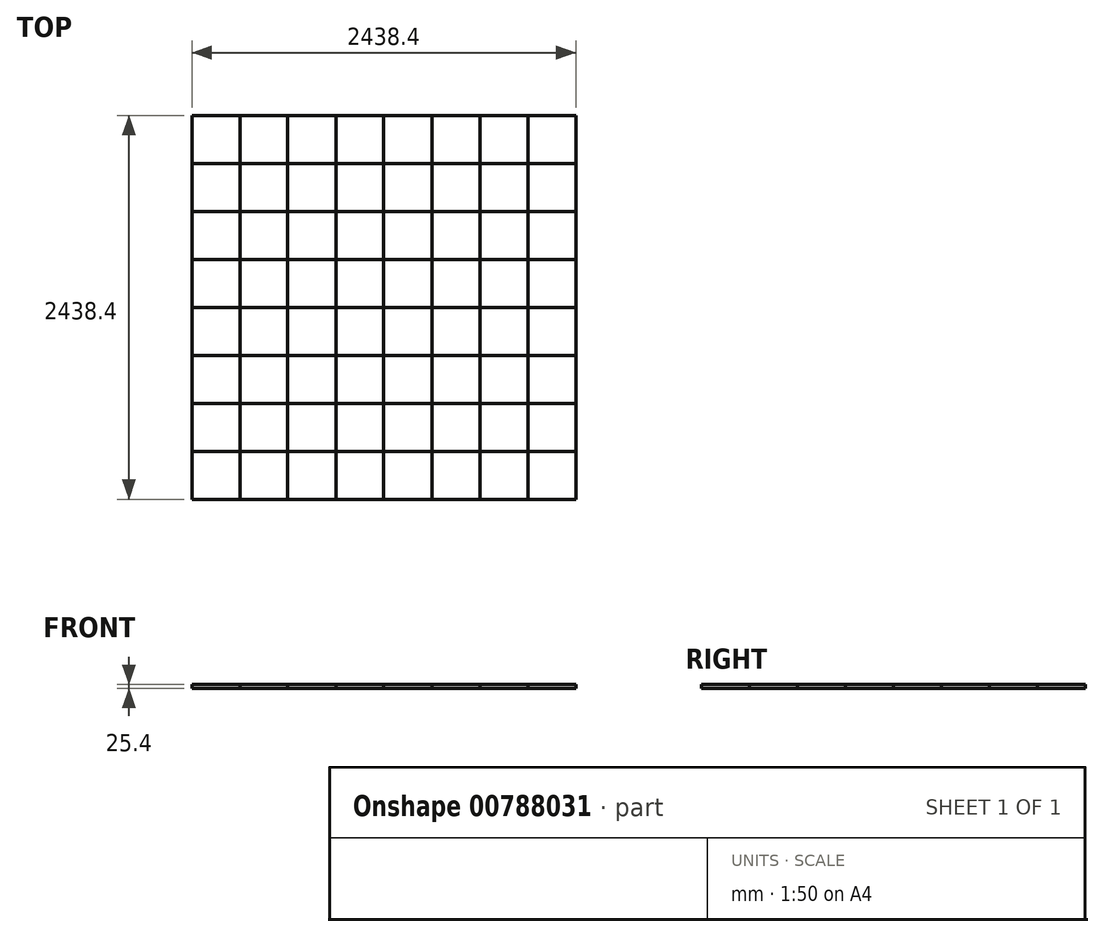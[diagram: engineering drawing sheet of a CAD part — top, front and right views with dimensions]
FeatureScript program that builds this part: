
annotation { "Feature Type Name" : "Feature", "Feature Type Description" : "" }
export const myFeature = defineFeature(function(context is Context, id is Id, definition is map)
    precondition{}
    {
        {
            var Q0;
            Q0=qCreatedBy(makeId("Top.planeOp"),FACE);
            var sketch = newSketch(context, id + "F0", { "sketchPlane" : qUnion([Q0])});
            skLineSegment(sketch, "E0.bottom", {"start": v(-1218.73, 1220.27) * mm, "end": v(1219.67, 1220.27) * mm});
            skLineSegment(sketch, "E0.top", {"start": v(-1218.73, -1218.13) * mm, "end": v(1219.67, -1218.13) * mm});
            skLineSegment(sketch, "E0.left", {"start": v(-1218.73, 1220.27) * mm, "end": v(-1218.73, -1218.13) * mm});
            skLineSegment(sketch, "E0.right", {"start": v(1219.67, 1220.27) * mm, "end": v(1219.67, -1218.13) * mm});
            skLineSegment(sketch, "E1", {"start": v(-913.93, -1218.13) * mm, "end": v(-913.93, 1220.27) * mm});
            skLineSegment(sketch, "E2", {"start": v(-609.13, 1229.92) * mm, "end": v(-609.13, -1218.13) * mm});
            skLineSegment(sketch, "E3", {"start": v(-304.33, -1218.13) * mm, "end": v(-304.33, 1220.27) * mm});
            skLineSegment(sketch, "E4", {"start": v(-609.13, 1220.27) * mm, "end": v(-609.13, -1218.13) * mm});
            skLineSegment(sketch, "E5", {"start": v(0.47, -1218.13) * mm, "end": v(0.47, 1220.27) * mm});
            skLineSegment(sketch, "E6", {"start": v(305.27, 1220.27) * mm, "end": v(305.27, -1218.13) * mm});
            skLineSegment(sketch, "E7", {"start": v(610.07, -1218.13) * mm, "end": v(610.07, 1220.27) * mm});
            skLineSegment(sketch, "E8", {"start": v(914.87, -1218.13) * mm, "end": v(914.87, 1220.27) * mm});
            skLineSegment(sketch, "E9", {"start": v(-1218.73, 915.47) * mm, "end": v(1219.67, 915.47) * mm});
            skLineSegment(sketch, "E10", {"start": v(1219.67, 610.67) * mm, "end": v(-1218.73, 610.67) * mm});
            skLineSegment(sketch, "E11", {"start": v(-1218.73, 305.87) * mm, "end": v(1219.67, 305.87) * mm});
            skLineSegment(sketch, "E12", {"start": v(1219.67, 1.07) * mm, "end": v(-1218.73, 1.07) * mm});
            skLineSegment(sketch, "E13", {"start": v(-1218.73, -303.73) * mm, "end": v(1219.67, -303.73) * mm});
            skLineSegment(sketch, "E14", {"start": v(1219.67, -608.53) * mm, "end": v(-1218.73, -608.53) * mm});
            skLineSegment(sketch, "E15", {"start": v(-1218.73, -913.33) * mm, "end": v(1219.67, -913.33) * mm});
            skSolve(sketch);
        }
        {
            var Q0;
            {var subQ0=sQuery(id+"F0.wireOp",EDGE,"E0.left");var subQ1=sQuery(id+"F0.wireOp",EDGE,"E0.top");var subQ2=makeQuery(id+"F0.imprint","INTERSECT",VERTEX,{"derivedFrom":[subQ1,subQ0]});Q0=makeQuery(id+"F0.imprint","IMPRINT",FACE,{"disambiguationData":[TD([[makeQuery(id+"F0.imprint","IMPRINT",EDGE,{"disambiguationData":[TD([[subQ2,-1.0]])],"derivedFrom":subQ1}),1.0]])]});}
            var Q1;
            {var subQ0=sQuery(id+"F0.wireOp",EDGE,"E15");var subQ1=sQuery(id+"F0.wireOp",EDGE,"E1");var subQ2=makeQuery(id+"F0.imprint","INTERSECT",VERTEX,{"derivedFrom":[subQ1,subQ0]});Q1=makeQuery(id+"F0.imprint","IMPRINT",FACE,{"disambiguationData":[TD([[makeQuery(id+"F0.imprint","IMPRINT",EDGE,{"disambiguationData":[TD([[subQ2,-1.0]])],"derivedFrom":subQ1}),-1.0]])]});}
            var Q2;
            {var subQ0=sQuery(id+"F0.wireOp",EDGE,"E3");var subQ1=sQuery(id+"F0.wireOp",EDGE,"E0.top");var subQ2=makeQuery(id+"F0.imprint","INTERSECT",VERTEX,{"derivedFrom":[subQ1,subQ0]});Q2=makeQuery(id+"F0.imprint","IMPRINT",FACE,{"disambiguationData":[TD([[makeQuery(id+"F0.imprint","IMPRINT",EDGE,{"disambiguationData":[TD([[subQ2,1.0]])],"derivedFrom":subQ1}),1.0]])]});}
            var Q3;
            {var subQ0=sQuery(id+"F0.wireOp",EDGE,"E15");var subQ1=sQuery(id+"F0.wireOp",EDGE,"E3");var subQ2=makeQuery(id+"F0.imprint","INTERSECT",VERTEX,{"derivedFrom":[subQ1,subQ0]});Q3=makeQuery(id+"F0.imprint","IMPRINT",FACE,{"disambiguationData":[TD([[makeQuery(id+"F0.imprint","IMPRINT",EDGE,{"disambiguationData":[TD([[subQ2,-1.0]])],"derivedFrom":subQ1}),-1.0]])]});}
            var Q4;
            {var subQ0=sQuery(id+"F0.wireOp",EDGE,"E5");var subQ1=sQuery(id+"F0.wireOp",EDGE,"E0.top");var subQ2=makeQuery(id+"F0.imprint","INTERSECT",VERTEX,{"derivedFrom":[subQ1,subQ0]});Q4=makeQuery(id+"F0.imprint","IMPRINT",FACE,{"disambiguationData":[TD([[makeQuery(id+"F0.imprint","IMPRINT",EDGE,{"disambiguationData":[TD([[subQ2,-1.0]])],"derivedFrom":subQ1}),1.0]])]});}
            var Q5;
            {var subQ0=sQuery(id+"F0.wireOp",EDGE,"E14");var subQ1=sQuery(id+"F0.wireOp",EDGE,"E6");var subQ2=makeQuery(id+"F0.imprint","INTERSECT",VERTEX,{"derivedFrom":[subQ1,subQ0]});Q5=makeQuery(id+"F0.imprint","IMPRINT",FACE,{"disambiguationData":[TD([[makeQuery(id+"F0.imprint","IMPRINT",EDGE,{"disambiguationData":[TD([[subQ2,-1.0]])],"derivedFrom":subQ1}),1.0]])]});}
            var Q6;
            {var subQ0=sQuery(id+"F0.wireOp",EDGE,"E7");var subQ1=sQuery(id+"F0.wireOp",EDGE,"E0.top");var subQ2=makeQuery(id+"F0.imprint","INTERSECT",VERTEX,{"derivedFrom":[subQ1,subQ0]});Q6=makeQuery(id+"F0.imprint","IMPRINT",FACE,{"disambiguationData":[TD([[makeQuery(id+"F0.imprint","IMPRINT",EDGE,{"disambiguationData":[TD([[subQ2,-1.0]])],"derivedFrom":subQ1}),1.0]])]});}
            var Q7;
            {var subQ0=sQuery(id+"F0.wireOp",EDGE,"E14");var subQ1=sQuery(id+"F0.wireOp",EDGE,"E0.right");var subQ2=makeQuery(id+"F0.imprint","INTERSECT",VERTEX,{"derivedFrom":[subQ1,subQ0]});Q7=makeQuery(id+"F0.imprint","IMPRINT",FACE,{"disambiguationData":[TD([[makeQuery(id+"F0.imprint","IMPRINT",EDGE,{"disambiguationData":[TD([[subQ2,-1.0]])],"derivedFrom":subQ1}),-1.0]])]});}
            var Q8;
            {var subQ0=sQuery(id+"F0.wireOp",EDGE,"E14");var subQ1=sQuery(id+"F0.wireOp",EDGE,"E7");var subQ2=makeQuery(id+"F0.imprint","INTERSECT",VERTEX,{"derivedFrom":[subQ1,subQ0]});Q8=makeQuery(id+"F0.imprint","IMPRINT",FACE,{"disambiguationData":[TD([[makeQuery(id+"F0.imprint","IMPRINT",EDGE,{"disambiguationData":[TD([[subQ2,-1.0]])],"derivedFrom":subQ1}),-1.0]])]});}
            var Q9;
            {var subQ0=sQuery(id+"F0.wireOp",EDGE,"E14");var subQ1=sQuery(id+"F0.wireOp",EDGE,"E5");var subQ2=makeQuery(id+"F0.imprint","INTERSECT",VERTEX,{"derivedFrom":[subQ1,subQ0]});Q9=makeQuery(id+"F0.imprint","IMPRINT",FACE,{"disambiguationData":[TD([[makeQuery(id+"F0.imprint","IMPRINT",EDGE,{"disambiguationData":[TD([[subQ2,-1.0]])],"derivedFrom":subQ1}),-1.0]])]});}
            var Q10;
            {var subQ0=sQuery(id+"F0.wireOp",EDGE,"E14");var subQ1=sQuery(id+"F0.wireOp",EDGE,"E3");var subQ2=makeQuery(id+"F0.imprint","INTERSECT",VERTEX,{"derivedFrom":[subQ1,subQ0]});Q10=makeQuery(id+"F0.imprint","IMPRINT",FACE,{"disambiguationData":[TD([[makeQuery(id+"F0.imprint","IMPRINT",EDGE,{"disambiguationData":[TD([[subQ2,-1.0]])],"derivedFrom":subQ1}),1.0]])]});}
            var Q11;
            {var subQ0=sQuery(id+"F0.wireOp",EDGE,"E13");var subQ1=sQuery(id+"F0.wireOp",EDGE,"E0.left");var subQ2=makeQuery(id+"F0.imprint","INTERSECT",VERTEX,{"derivedFrom":[subQ1,subQ0]});Q11=makeQuery(id+"F0.imprint","IMPRINT",FACE,{"disambiguationData":[TD([[makeQuery(id+"F0.imprint","IMPRINT",EDGE,{"disambiguationData":[TD([[subQ2,-1.0]])],"derivedFrom":subQ1}),1.0]])]});}
            var Q12;
            {var subQ0=sQuery(id+"F0.wireOp",EDGE,"E13");var subQ1=sQuery(id+"F0.wireOp",EDGE,"E1");var subQ2=makeQuery(id+"F0.imprint","INTERSECT",VERTEX,{"derivedFrom":[subQ1,subQ0]});Q12=makeQuery(id+"F0.imprint","IMPRINT",FACE,{"disambiguationData":[TD([[makeQuery(id+"F0.imprint","IMPRINT",EDGE,{"disambiguationData":[TD([[subQ2,-1.0]])],"derivedFrom":subQ1}),-1.0]])]});}
            var Q13;
            {var subQ0=sQuery(id+"F0.wireOp",EDGE,"E13");var subQ1=sQuery(id+"F0.wireOp",EDGE,"E3");var subQ2=makeQuery(id+"F0.imprint","INTERSECT",VERTEX,{"derivedFrom":[subQ1,subQ0]});Q13=makeQuery(id+"F0.imprint","IMPRINT",FACE,{"disambiguationData":[TD([[makeQuery(id+"F0.imprint","IMPRINT",EDGE,{"disambiguationData":[TD([[subQ2,-1.0]])],"derivedFrom":subQ1}),-1.0]])]});}
            var Q14;
            {var subQ0=sQuery(id+"F0.wireOp",EDGE,"E12");var subQ1=sQuery(id+"F0.wireOp",EDGE,"E6");var subQ2=makeQuery(id+"F0.imprint","INTERSECT",VERTEX,{"derivedFrom":[subQ1,subQ0]});Q14=makeQuery(id+"F0.imprint","IMPRINT",FACE,{"disambiguationData":[TD([[makeQuery(id+"F0.imprint","IMPRINT",EDGE,{"disambiguationData":[TD([[subQ2,-1.0]])],"derivedFrom":subQ1}),1.0]])]});}
            var Q15;
            {var subQ0=sQuery(id+"F0.wireOp",EDGE,"E12");var subQ1=sQuery(id+"F0.wireOp",EDGE,"E0.right");var subQ2=makeQuery(id+"F0.imprint","INTERSECT",VERTEX,{"derivedFrom":[subQ1,subQ0]});Q15=makeQuery(id+"F0.imprint","IMPRINT",FACE,{"disambiguationData":[TD([[makeQuery(id+"F0.imprint","IMPRINT",EDGE,{"disambiguationData":[TD([[subQ2,-1.0]])],"derivedFrom":subQ1}),-1.0]])]});}
            var Q16;
            {var subQ0=sQuery(id+"F0.wireOp",EDGE,"E12");var subQ1=sQuery(id+"F0.wireOp",EDGE,"E7");var subQ2=makeQuery(id+"F0.imprint","INTERSECT",VERTEX,{"derivedFrom":[subQ1,subQ0]});Q16=makeQuery(id+"F0.imprint","IMPRINT",FACE,{"disambiguationData":[TD([[makeQuery(id+"F0.imprint","IMPRINT",EDGE,{"disambiguationData":[TD([[subQ2,-1.0]])],"derivedFrom":subQ1}),-1.0]])]});}
            var Q17;
            {var subQ0=sQuery(id+"F0.wireOp",EDGE,"E10");var subQ1=sQuery(id+"F0.wireOp",EDGE,"E0.right");var subQ2=makeQuery(id+"F0.imprint","INTERSECT",VERTEX,{"derivedFrom":[subQ1,subQ0]});Q17=makeQuery(id+"F0.imprint","IMPRINT",FACE,{"disambiguationData":[TD([[makeQuery(id+"F0.imprint","IMPRINT",EDGE,{"disambiguationData":[TD([[subQ2,-1.0]])],"derivedFrom":subQ1}),-1.0]])]});}
            var Q18;
            {var subQ0=sQuery(id+"F0.wireOp",EDGE,"E10");var subQ1=sQuery(id+"F0.wireOp",EDGE,"E7");var subQ2=makeQuery(id+"F0.imprint","INTERSECT",VERTEX,{"derivedFrom":[subQ1,subQ0]});Q18=makeQuery(id+"F0.imprint","IMPRINT",FACE,{"disambiguationData":[TD([[makeQuery(id+"F0.imprint","IMPRINT",EDGE,{"disambiguationData":[TD([[subQ2,-1.0]])],"derivedFrom":subQ1}),-1.0]])]});}
            var Q19;
            {var subQ0=sQuery(id+"F0.wireOp",EDGE,"E0.right");var subQ1=sQuery(id+"F0.wireOp",EDGE,"E0.bottom");var subQ2=makeQuery(id+"F0.imprint","INTERSECT",VERTEX,{"derivedFrom":[subQ1,subQ0]});Q19=makeQuery(id+"F0.imprint","IMPRINT",FACE,{"disambiguationData":[TD([[makeQuery(id+"F0.imprint","IMPRINT",EDGE,{"disambiguationData":[TD([[subQ2,1.0]])],"derivedFrom":subQ1}),-1.0]])]});}
            var Q20;
            {var subQ0=sQuery(id+"F0.wireOp",EDGE,"E6");var subQ1=sQuery(id+"F0.wireOp",EDGE,"E0.bottom");var subQ2=makeQuery(id+"F0.imprint","INTERSECT",VERTEX,{"derivedFrom":[subQ1,subQ0]});Q20=makeQuery(id+"F0.imprint","IMPRINT",FACE,{"disambiguationData":[TD([[makeQuery(id+"F0.imprint","IMPRINT",EDGE,{"disambiguationData":[TD([[subQ2,-1.0]])],"derivedFrom":subQ1}),-1.0]])]});}
            var Q21;
            {var subQ0=sQuery(id+"F0.wireOp",EDGE,"E10");var subQ1=sQuery(id+"F0.wireOp",EDGE,"E6");var subQ2=makeQuery(id+"F0.imprint","INTERSECT",VERTEX,{"derivedFrom":[subQ1,subQ0]});Q21=makeQuery(id+"F0.imprint","IMPRINT",FACE,{"disambiguationData":[TD([[makeQuery(id+"F0.imprint","IMPRINT",EDGE,{"disambiguationData":[TD([[subQ2,-1.0]])],"derivedFrom":subQ1}),1.0]])]});}
            var Q22;
            {var subQ0=sQuery(id+"F0.wireOp",EDGE,"E12");var subQ1=sQuery(id+"F0.wireOp",EDGE,"E5");var subQ2=makeQuery(id+"F0.imprint","INTERSECT",VERTEX,{"derivedFrom":[subQ1,subQ0]});Q22=makeQuery(id+"F0.imprint","IMPRINT",FACE,{"disambiguationData":[TD([[makeQuery(id+"F0.imprint","IMPRINT",EDGE,{"disambiguationData":[TD([[subQ2,-1.0]])],"derivedFrom":subQ1}),-1.0]])]});}
            var Q23;
            {var subQ0=sQuery(id+"F0.wireOp",EDGE,"E10");var subQ1=sQuery(id+"F0.wireOp",EDGE,"E5");var subQ2=makeQuery(id+"F0.imprint","INTERSECT",VERTEX,{"derivedFrom":[subQ1,subQ0]});Q23=makeQuery(id+"F0.imprint","IMPRINT",FACE,{"disambiguationData":[TD([[makeQuery(id+"F0.imprint","IMPRINT",EDGE,{"disambiguationData":[TD([[subQ2,-1.0]])],"derivedFrom":subQ1}),-1.0]])]});}
            var Q24;
            {var subQ0=sQuery(id+"F0.wireOp",EDGE,"E3");var subQ1=sQuery(id+"F0.wireOp",EDGE,"E0.bottom");var subQ2=makeQuery(id+"F0.imprint","INTERSECT",VERTEX,{"derivedFrom":[subQ1,subQ0]});Q24=makeQuery(id+"F0.imprint","IMPRINT",FACE,{"disambiguationData":[TD([[makeQuery(id+"F0.imprint","IMPRINT",EDGE,{"disambiguationData":[TD([[subQ2,-1.0]])],"derivedFrom":subQ1}),-1.0]])]});}
            var Q25;
            {var subQ0=sQuery(id+"F0.wireOp",EDGE,"E11");var subQ1=sQuery(id+"F0.wireOp",EDGE,"E3");var subQ2=makeQuery(id+"F0.imprint","INTERSECT",VERTEX,{"derivedFrom":[subQ1,subQ0]});Q25=makeQuery(id+"F0.imprint","IMPRINT",FACE,{"disambiguationData":[TD([[makeQuery(id+"F0.imprint","IMPRINT",EDGE,{"disambiguationData":[TD([[subQ2,-1.0]])],"derivedFrom":subQ1}),-1.0]])]});}
            var Q26;
            {var subQ0=sQuery(id+"F0.wireOp",EDGE,"E12");var subQ1=sQuery(id+"F0.wireOp",EDGE,"E3");var subQ2=makeQuery(id+"F0.imprint","INTERSECT",VERTEX,{"derivedFrom":[subQ1,subQ0]});Q26=makeQuery(id+"F0.imprint","IMPRINT",FACE,{"disambiguationData":[TD([[makeQuery(id+"F0.imprint","IMPRINT",EDGE,{"disambiguationData":[TD([[subQ2,-1.0]])],"derivedFrom":subQ1}),1.0]])]});}
            var Q27;
            {var subQ0=sQuery(id+"F0.wireOp",EDGE,"E10");var subQ1=sQuery(id+"F0.wireOp",EDGE,"E3");var subQ2=makeQuery(id+"F0.imprint","INTERSECT",VERTEX,{"derivedFrom":[subQ1,subQ0]});Q27=makeQuery(id+"F0.imprint","IMPRINT",FACE,{"disambiguationData":[TD([[makeQuery(id+"F0.imprint","IMPRINT",EDGE,{"disambiguationData":[TD([[subQ2,-1.0]])],"derivedFrom":subQ1}),1.0]])]});}
            var Q28;
            {var subQ0=sQuery(id+"F0.wireOp",EDGE,"E1");var subQ1=sQuery(id+"F0.wireOp",EDGE,"E0.bottom");var subQ2=makeQuery(id+"F0.imprint","INTERSECT",VERTEX,{"derivedFrom":[subQ1,subQ0]});Q28=makeQuery(id+"F0.imprint","IMPRINT",FACE,{"disambiguationData":[TD([[makeQuery(id+"F0.imprint","IMPRINT",EDGE,{"disambiguationData":[TD([[subQ2,-1.0]])],"derivedFrom":subQ1}),-1.0]])]});}
            var Q29;
            {var subQ0=sQuery(id+"F0.wireOp",EDGE,"E11");var subQ1=sQuery(id+"F0.wireOp",EDGE,"E1");var subQ2=makeQuery(id+"F0.imprint","INTERSECT",VERTEX,{"derivedFrom":[subQ1,subQ0]});Q29=makeQuery(id+"F0.imprint","IMPRINT",FACE,{"disambiguationData":[TD([[makeQuery(id+"F0.imprint","IMPRINT",EDGE,{"disambiguationData":[TD([[subQ2,-1.0]])],"derivedFrom":subQ1}),-1.0]])]});}
            var Q30;
            {var subQ0=sQuery(id+"F0.wireOp",EDGE,"E11");var subQ1=sQuery(id+"F0.wireOp",EDGE,"E0.left");var subQ2=makeQuery(id+"F0.imprint","INTERSECT",VERTEX,{"derivedFrom":[subQ1,subQ0]});Q30=makeQuery(id+"F0.imprint","IMPRINT",FACE,{"disambiguationData":[TD([[makeQuery(id+"F0.imprint","IMPRINT",EDGE,{"disambiguationData":[TD([[subQ2,-1.0]])],"derivedFrom":subQ1}),1.0]])]});}
            var Q31;
            {var subQ0=sQuery(id+"F0.wireOp",EDGE,"E9");var subQ1=sQuery(id+"F0.wireOp",EDGE,"E0.left");var subQ2=makeQuery(id+"F0.imprint","INTERSECT",VERTEX,{"derivedFrom":[subQ1,subQ0]});Q31=makeQuery(id+"F0.imprint","IMPRINT",FACE,{"disambiguationData":[TD([[makeQuery(id+"F0.imprint","IMPRINT",EDGE,{"disambiguationData":[TD([[subQ2,-1.0]])],"derivedFrom":subQ1}),1.0]])]});}
            extrude(context, id + "F1", {"entities" : qUnion([Q0, Q1, Q2, Q3, Q4, Q5, Q6, Q7, Q8, Q9, Q10, Q11, Q12, Q13, Q14, Q15, Q16, Q17, Q18, Q19, Q20, Q21, Q22, Q23, Q24, Q25, Q26, Q27, Q28, Q29, Q30, Q31]), "depth" : 25.4 * mm, "offsetDistance" : 25.4 * mm});
        }
        {
            var Q0;
            {var subQ0=sQuery(id+"F0.wireOp",EDGE,"E1");var subQ1=sQuery(id+"F0.wireOp",EDGE,"E0.top");var subQ2=makeQuery(id+"F0.imprint","INTERSECT",VERTEX,{"derivedFrom":[subQ1,subQ0]});Q0=makeQuery(id+"F0.imprint","IMPRINT",FACE,{"disambiguationData":[TD([[makeQuery(id+"F0.imprint","IMPRINT",EDGE,{"disambiguationData":[TD([[subQ2,-1.0]])],"derivedFrom":subQ1}),1.0]])]});}
            var Q1;
            {var subQ0=sQuery(id+"F0.wireOp",EDGE,"E14");var subQ1=sQuery(id+"F0.wireOp",EDGE,"E0.left");var subQ2=makeQuery(id+"F0.imprint","INTERSECT",VERTEX,{"derivedFrom":[subQ1,subQ0]});Q1=makeQuery(id+"F0.imprint","IMPRINT",FACE,{"disambiguationData":[TD([[makeQuery(id+"F0.imprint","IMPRINT",EDGE,{"disambiguationData":[TD([[subQ2,-1.0]])],"derivedFrom":subQ1}),1.0]])]});}
            var Q2;
            {var subQ0=sQuery(id+"F0.wireOp",EDGE,"E15");var subQ1=sQuery(id+"F0.wireOp",EDGE,"E3");var subQ2=makeQuery(id+"F0.imprint","INTERSECT",VERTEX,{"derivedFrom":[subQ1,subQ0]});Q2=makeQuery(id+"F0.imprint","IMPRINT",FACE,{"disambiguationData":[TD([[makeQuery(id+"F0.imprint","IMPRINT",EDGE,{"disambiguationData":[TD([[subQ2,-1.0]])],"derivedFrom":subQ1}),1.0]])]});}
            var Q3;
            {var subQ0=sQuery(id+"F0.wireOp",EDGE,"E3");var subQ1=sQuery(id+"F0.wireOp",EDGE,"E0.top");var subQ2=makeQuery(id+"F0.imprint","INTERSECT",VERTEX,{"derivedFrom":[subQ1,subQ0]});Q3=makeQuery(id+"F0.imprint","IMPRINT",FACE,{"disambiguationData":[TD([[makeQuery(id+"F0.imprint","IMPRINT",EDGE,{"disambiguationData":[TD([[subQ2,-1.0]])],"derivedFrom":subQ1}),1.0]])]});}
            var Q4;
            {var subQ0=sQuery(id+"F0.wireOp",EDGE,"E15");var subQ1=sQuery(id+"F0.wireOp",EDGE,"E5");var subQ2=makeQuery(id+"F0.imprint","INTERSECT",VERTEX,{"derivedFrom":[subQ1,subQ0]});Q4=makeQuery(id+"F0.imprint","IMPRINT",FACE,{"disambiguationData":[TD([[makeQuery(id+"F0.imprint","IMPRINT",EDGE,{"disambiguationData":[TD([[subQ2,-1.0]])],"derivedFrom":subQ1}),-1.0]])]});}
            var Q5;
            {var subQ0=sQuery(id+"F0.wireOp",EDGE,"E6");var subQ1=sQuery(id+"F0.wireOp",EDGE,"E0.top");var subQ2=makeQuery(id+"F0.imprint","INTERSECT",VERTEX,{"derivedFrom":[subQ1,subQ0]});Q5=makeQuery(id+"F0.imprint","IMPRINT",FACE,{"disambiguationData":[TD([[makeQuery(id+"F0.imprint","IMPRINT",EDGE,{"disambiguationData":[TD([[subQ2,-1.0]])],"derivedFrom":subQ1}),1.0]])]});}
            var Q6;
            {var subQ0=sQuery(id+"F0.wireOp",EDGE,"E15");var subQ1=sQuery(id+"F0.wireOp",EDGE,"E7");var subQ2=makeQuery(id+"F0.imprint","INTERSECT",VERTEX,{"derivedFrom":[subQ1,subQ0]});Q6=makeQuery(id+"F0.imprint","IMPRINT",FACE,{"disambiguationData":[TD([[makeQuery(id+"F0.imprint","IMPRINT",EDGE,{"disambiguationData":[TD([[subQ2,-1.0]])],"derivedFrom":subQ1}),-1.0]])]});}
            var Q7;
            {var subQ0=sQuery(id+"F0.wireOp",EDGE,"E0.right");var subQ1=sQuery(id+"F0.wireOp",EDGE,"E0.top");var subQ2=makeQuery(id+"F0.imprint","INTERSECT",VERTEX,{"derivedFrom":[subQ1,subQ0]});Q7=makeQuery(id+"F0.imprint","IMPRINT",FACE,{"disambiguationData":[TD([[makeQuery(id+"F0.imprint","IMPRINT",EDGE,{"disambiguationData":[TD([[subQ2,1.0]])],"derivedFrom":subQ1}),1.0]])]});}
            var Q8;
            {var subQ0=sQuery(id+"F0.wireOp",EDGE,"E13");var subQ1=sQuery(id+"F0.wireOp",EDGE,"E0.right");var subQ2=makeQuery(id+"F0.imprint","INTERSECT",VERTEX,{"derivedFrom":[subQ1,subQ0]});Q8=makeQuery(id+"F0.imprint","IMPRINT",FACE,{"disambiguationData":[TD([[makeQuery(id+"F0.imprint","IMPRINT",EDGE,{"disambiguationData":[TD([[subQ2,-1.0]])],"derivedFrom":subQ1}),-1.0]])]});}
            var Q9;
            {var subQ0=sQuery(id+"F0.wireOp",EDGE,"E13");var subQ1=sQuery(id+"F0.wireOp",EDGE,"E7");var subQ2=makeQuery(id+"F0.imprint","INTERSECT",VERTEX,{"derivedFrom":[subQ1,subQ0]});Q9=makeQuery(id+"F0.imprint","IMPRINT",FACE,{"disambiguationData":[TD([[makeQuery(id+"F0.imprint","IMPRINT",EDGE,{"disambiguationData":[TD([[subQ2,-1.0]])],"derivedFrom":subQ1}),-1.0]])]});}
            var Q10;
            {var subQ0=sQuery(id+"F0.wireOp",EDGE,"E13");var subQ1=sQuery(id+"F0.wireOp",EDGE,"E6");var subQ2=makeQuery(id+"F0.imprint","INTERSECT",VERTEX,{"derivedFrom":[subQ1,subQ0]});Q10=makeQuery(id+"F0.imprint","IMPRINT",FACE,{"disambiguationData":[TD([[makeQuery(id+"F0.imprint","IMPRINT",EDGE,{"disambiguationData":[TD([[subQ2,-1.0]])],"derivedFrom":subQ1}),1.0]])]});}
            var Q11;
            {var subQ0=sQuery(id+"F0.wireOp",EDGE,"E13");var subQ1=sQuery(id+"F0.wireOp",EDGE,"E5");var subQ2=makeQuery(id+"F0.imprint","INTERSECT",VERTEX,{"derivedFrom":[subQ1,subQ0]});Q11=makeQuery(id+"F0.imprint","IMPRINT",FACE,{"disambiguationData":[TD([[makeQuery(id+"F0.imprint","IMPRINT",EDGE,{"disambiguationData":[TD([[subQ2,-1.0]])],"derivedFrom":subQ1}),-1.0]])]});}
            var Q12;
            {var subQ0=sQuery(id+"F0.wireOp",EDGE,"E14");var subQ1=sQuery(id+"F0.wireOp",EDGE,"E3");var subQ2=makeQuery(id+"F0.imprint","INTERSECT",VERTEX,{"derivedFrom":[subQ1,subQ0]});Q12=makeQuery(id+"F0.imprint","IMPRINT",FACE,{"disambiguationData":[TD([[makeQuery(id+"F0.imprint","IMPRINT",EDGE,{"disambiguationData":[TD([[subQ2,-1.0]])],"derivedFrom":subQ1}),-1.0]])]});}
            var Q13;
            {var subQ0=sQuery(id+"F0.wireOp",EDGE,"E14");var subQ1=sQuery(id+"F0.wireOp",EDGE,"E1");var subQ2=makeQuery(id+"F0.imprint","INTERSECT",VERTEX,{"derivedFrom":[subQ1,subQ0]});Q13=makeQuery(id+"F0.imprint","IMPRINT",FACE,{"disambiguationData":[TD([[makeQuery(id+"F0.imprint","IMPRINT",EDGE,{"disambiguationData":[TD([[subQ2,-1.0]])],"derivedFrom":subQ1}),-1.0]])]});}
            var Q14;
            {var subQ0=sQuery(id+"F0.wireOp",EDGE,"E13");var subQ1=sQuery(id+"F0.wireOp",EDGE,"E3");var subQ2=makeQuery(id+"F0.imprint","INTERSECT",VERTEX,{"derivedFrom":[subQ1,subQ0]});Q14=makeQuery(id+"F0.imprint","IMPRINT",FACE,{"disambiguationData":[TD([[makeQuery(id+"F0.imprint","IMPRINT",EDGE,{"disambiguationData":[TD([[subQ2,-1.0]])],"derivedFrom":subQ1}),1.0]])]});}
            var Q15;
            {var subQ0=sQuery(id+"F0.wireOp",EDGE,"E12");var subQ1=sQuery(id+"F0.wireOp",EDGE,"E0.left");var subQ2=makeQuery(id+"F0.imprint","INTERSECT",VERTEX,{"derivedFrom":[subQ1,subQ0]});Q15=makeQuery(id+"F0.imprint","IMPRINT",FACE,{"disambiguationData":[TD([[makeQuery(id+"F0.imprint","IMPRINT",EDGE,{"disambiguationData":[TD([[subQ2,-1.0]])],"derivedFrom":subQ1}),1.0]])]});}
            var Q16;
            {var subQ0=sQuery(id+"F0.wireOp",EDGE,"E12");var subQ1=sQuery(id+"F0.wireOp",EDGE,"E1");var subQ2=makeQuery(id+"F0.imprint","INTERSECT",VERTEX,{"derivedFrom":[subQ1,subQ0]});Q16=makeQuery(id+"F0.imprint","IMPRINT",FACE,{"disambiguationData":[TD([[makeQuery(id+"F0.imprint","IMPRINT",EDGE,{"disambiguationData":[TD([[subQ2,-1.0]])],"derivedFrom":subQ1}),-1.0]])]});}
            var Q17;
            {var subQ0=sQuery(id+"F0.wireOp",EDGE,"E10");var subQ1=sQuery(id+"F0.wireOp",EDGE,"E0.left");var subQ2=makeQuery(id+"F0.imprint","INTERSECT",VERTEX,{"derivedFrom":[subQ1,subQ0]});Q17=makeQuery(id+"F0.imprint","IMPRINT",FACE,{"disambiguationData":[TD([[makeQuery(id+"F0.imprint","IMPRINT",EDGE,{"disambiguationData":[TD([[subQ2,-1.0]])],"derivedFrom":subQ1}),1.0]])]});}
            var Q18;
            {var subQ0=sQuery(id+"F0.wireOp",EDGE,"E10");var subQ1=sQuery(id+"F0.wireOp",EDGE,"E1");var subQ2=makeQuery(id+"F0.imprint","INTERSECT",VERTEX,{"derivedFrom":[subQ1,subQ0]});Q18=makeQuery(id+"F0.imprint","IMPRINT",FACE,{"disambiguationData":[TD([[makeQuery(id+"F0.imprint","IMPRINT",EDGE,{"disambiguationData":[TD([[subQ2,-1.0]])],"derivedFrom":subQ1}),-1.0]])]});}
            var Q19;
            {var subQ0=sQuery(id+"F0.wireOp",EDGE,"E11");var subQ1=sQuery(id+"F0.wireOp",EDGE,"E3");var subQ2=makeQuery(id+"F0.imprint","INTERSECT",VERTEX,{"derivedFrom":[subQ1,subQ0]});Q19=makeQuery(id+"F0.imprint","IMPRINT",FACE,{"disambiguationData":[TD([[makeQuery(id+"F0.imprint","IMPRINT",EDGE,{"disambiguationData":[TD([[subQ2,-1.0]])],"derivedFrom":subQ1}),1.0]])]});}
            var Q20;
            {var subQ0=sQuery(id+"F0.wireOp",EDGE,"E12");var subQ1=sQuery(id+"F0.wireOp",EDGE,"E3");var subQ2=makeQuery(id+"F0.imprint","INTERSECT",VERTEX,{"derivedFrom":[subQ1,subQ0]});Q20=makeQuery(id+"F0.imprint","IMPRINT",FACE,{"disambiguationData":[TD([[makeQuery(id+"F0.imprint","IMPRINT",EDGE,{"disambiguationData":[TD([[subQ2,-1.0]])],"derivedFrom":subQ1}),-1.0]])]});}
            var Q21;
            {var subQ0=sQuery(id+"F0.wireOp",EDGE,"E11");var subQ1=sQuery(id+"F0.wireOp",EDGE,"E5");var subQ2=makeQuery(id+"F0.imprint","INTERSECT",VERTEX,{"derivedFrom":[subQ1,subQ0]});Q21=makeQuery(id+"F0.imprint","IMPRINT",FACE,{"disambiguationData":[TD([[makeQuery(id+"F0.imprint","IMPRINT",EDGE,{"disambiguationData":[TD([[subQ2,-1.0]])],"derivedFrom":subQ1}),-1.0]])]});}
            var Q22;
            {var subQ0=sQuery(id+"F0.wireOp",EDGE,"E11");var subQ1=sQuery(id+"F0.wireOp",EDGE,"E6");var subQ2=makeQuery(id+"F0.imprint","INTERSECT",VERTEX,{"derivedFrom":[subQ1,subQ0]});Q22=makeQuery(id+"F0.imprint","IMPRINT",FACE,{"disambiguationData":[TD([[makeQuery(id+"F0.imprint","IMPRINT",EDGE,{"disambiguationData":[TD([[subQ2,-1.0]])],"derivedFrom":subQ1}),1.0]])]});}
            var Q23;
            {var subQ0=sQuery(id+"F0.wireOp",EDGE,"E11");var subQ1=sQuery(id+"F0.wireOp",EDGE,"E7");var subQ2=makeQuery(id+"F0.imprint","INTERSECT",VERTEX,{"derivedFrom":[subQ1,subQ0]});Q23=makeQuery(id+"F0.imprint","IMPRINT",FACE,{"disambiguationData":[TD([[makeQuery(id+"F0.imprint","IMPRINT",EDGE,{"disambiguationData":[TD([[subQ2,-1.0]])],"derivedFrom":subQ1}),-1.0]])]});}
            var Q24;
            {var subQ0=sQuery(id+"F0.wireOp",EDGE,"E11");var subQ1=sQuery(id+"F0.wireOp",EDGE,"E0.right");var subQ2=makeQuery(id+"F0.imprint","INTERSECT",VERTEX,{"derivedFrom":[subQ1,subQ0]});Q24=makeQuery(id+"F0.imprint","IMPRINT",FACE,{"disambiguationData":[TD([[makeQuery(id+"F0.imprint","IMPRINT",EDGE,{"disambiguationData":[TD([[subQ2,-1.0]])],"derivedFrom":subQ1}),-1.0]])]});}
            var Q25;
            {var subQ0=sQuery(id+"F0.wireOp",EDGE,"E9");var subQ1=sQuery(id+"F0.wireOp",EDGE,"E6");var subQ2=makeQuery(id+"F0.imprint","INTERSECT",VERTEX,{"derivedFrom":[subQ1,subQ0]});Q25=makeQuery(id+"F0.imprint","IMPRINT",FACE,{"disambiguationData":[TD([[makeQuery(id+"F0.imprint","IMPRINT",EDGE,{"disambiguationData":[TD([[subQ2,-1.0]])],"derivedFrom":subQ1}),1.0]])]});}
            var Q26;
            {var subQ0=sQuery(id+"F0.wireOp",EDGE,"E10");var subQ1=sQuery(id+"F0.wireOp",EDGE,"E3");var subQ2=makeQuery(id+"F0.imprint","INTERSECT",VERTEX,{"derivedFrom":[subQ1,subQ0]});Q26=makeQuery(id+"F0.imprint","IMPRINT",FACE,{"disambiguationData":[TD([[makeQuery(id+"F0.imprint","IMPRINT",EDGE,{"disambiguationData":[TD([[subQ2,-1.0]])],"derivedFrom":subQ1}),-1.0]])]});}
            var Q27;
            {var subQ0=sQuery(id+"F0.wireOp",EDGE,"E4");var subQ1=sQuery(id+"F0.wireOp",EDGE,"E0.bottom");var subQ2=makeQuery(id+"F0.imprint","INTERSECT",VERTEX,{"derivedFrom":[subQ1,subQ0]});Q27=makeQuery(id+"F0.imprint","IMPRINT",FACE,{"disambiguationData":[TD([[makeQuery(id+"F0.imprint","IMPRINT",EDGE,{"disambiguationData":[TD([[subQ2,-1.0]])],"derivedFrom":subQ1}),-1.0]])]});}
            var Q28;
            {var subQ0=sQuery(id+"F0.wireOp",EDGE,"E5");var subQ1=sQuery(id+"F0.wireOp",EDGE,"E0.bottom");var subQ2=makeQuery(id+"F0.imprint","INTERSECT",VERTEX,{"derivedFrom":[subQ1,subQ0]});Q28=makeQuery(id+"F0.imprint","IMPRINT",FACE,{"disambiguationData":[TD([[makeQuery(id+"F0.imprint","IMPRINT",EDGE,{"disambiguationData":[TD([[subQ2,-1.0]])],"derivedFrom":subQ1}),-1.0]])]});}
            var Q29;
            {var subQ0=sQuery(id+"F0.wireOp",EDGE,"E7");var subQ1=sQuery(id+"F0.wireOp",EDGE,"E0.bottom");var subQ2=makeQuery(id+"F0.imprint","INTERSECT",VERTEX,{"derivedFrom":[subQ1,subQ0]});Q29=makeQuery(id+"F0.imprint","IMPRINT",FACE,{"disambiguationData":[TD([[makeQuery(id+"F0.imprint","IMPRINT",EDGE,{"disambiguationData":[TD([[subQ2,-1.0]])],"derivedFrom":subQ1}),-1.0]])]});}
            var Q30;
            {var subQ0=sQuery(id+"F0.wireOp",EDGE,"E0.left");var subQ1=sQuery(id+"F0.wireOp",EDGE,"E0.bottom");var subQ2=makeQuery(id+"F0.imprint","INTERSECT",VERTEX,{"derivedFrom":[subQ1,subQ0]});Q30=makeQuery(id+"F0.imprint","IMPRINT",FACE,{"disambiguationData":[TD([[makeQuery(id+"F0.imprint","IMPRINT",EDGE,{"disambiguationData":[TD([[subQ2,-1.0]])],"derivedFrom":subQ1}),-1.0]])]});}
            var Q31;
            {var subQ0=sQuery(id+"F0.wireOp",EDGE,"E9");var subQ1=sQuery(id+"F0.wireOp",EDGE,"E0.right");var subQ2=makeQuery(id+"F0.imprint","INTERSECT",VERTEX,{"derivedFrom":[subQ1,subQ0]});Q31=makeQuery(id+"F0.imprint","IMPRINT",FACE,{"disambiguationData":[TD([[makeQuery(id+"F0.imprint","IMPRINT",EDGE,{"disambiguationData":[TD([[subQ2,-1.0]])],"derivedFrom":subQ1}),-1.0]])]});}
            extrude(context, id + "F2", {"entities" : qUnion([Q0, Q1, Q2, Q3, Q4, Q5, Q6, Q7, Q8, Q9, Q10, Q11, Q12, Q13, Q14, Q15, Q16, Q17, Q18, Q19, Q20, Q21, Q22, Q23, Q24, Q25, Q26, Q27, Q28, Q29, Q30, Q31]), "depth" : 25.4 * mm, "offsetDistance" : 25.4 * mm});
        }
    });
